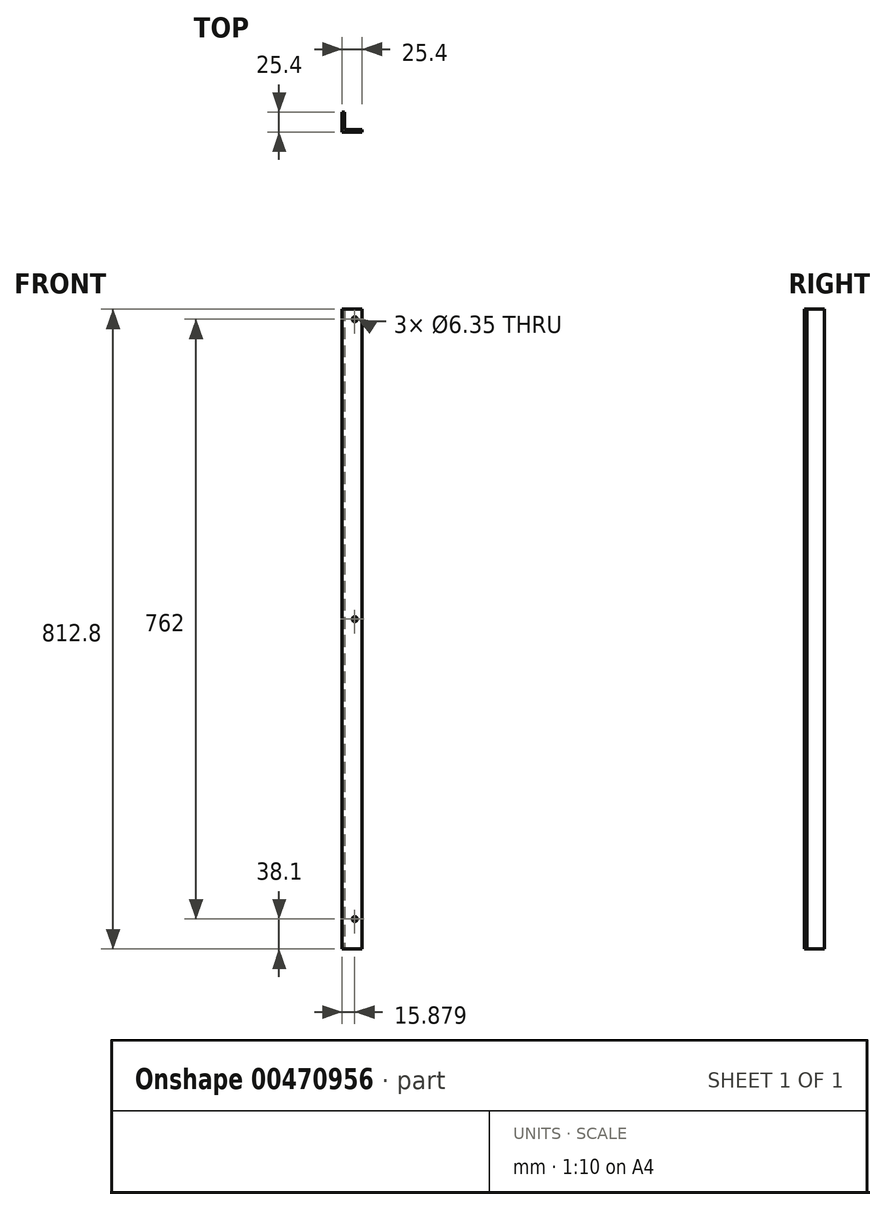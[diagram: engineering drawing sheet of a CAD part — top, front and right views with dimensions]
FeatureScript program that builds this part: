
annotation { "Feature Type Name" : "Feature", "Feature Type Description" : "" }
export const myFeature = defineFeature(function(context is Context, id is Id, definition is map)
    precondition{}
    {
        {
            var Q0;
            Q0=qCreatedBy(makeId("Top.planeOp"),FACE);
            var sketch = newSketch(context, id + "F0", { "sketchPlane" : qUnion([Q0])});
            skLineSegment(sketch, "E0", {"start": v(-9.08, 8.68) * mm, "end": v(-9.08, -16.72) * mm});
            skLineSegment(sketch, "E1", {"start": v(-9.08, -16.72) * mm, "end": v(16.32, -16.72) * mm});
            skLineSegment(sketch, "E2", {"start": v(16.32, -16.72) * mm, "end": v(16.32, -13.54) * mm});
            skLineSegment(sketch, "E3", {"start": v(16.32, -13.54) * mm, "end": v(-5.9, -13.54) * mm});
            skLineSegment(sketch, "E4", {"start": v(-5.9, -13.54) * mm, "end": v(-5.9, 8.68) * mm});
            skLineSegment(sketch, "E5", {"start": v(-5.9, 8.68) * mm, "end": v(-9.08, 8.68) * mm});
            skSolve(sketch);
        }
        {
            var Q0;
            Q0=makeQuery(id+"F0.imprint","IMPRINT",FACE,{"disambiguationData":[TD([[makeQuery(id+"F0.imprint","IMPRINT",EDGE,{"derivedFrom":sQuery(id+"F0.wireOp",EDGE,"E0")}),1.0]])]});
            extrude(context, id + "F1", {"entities" : qUnion([Q0]), "depth" : 812.8 * mm});
        }
        {
            var Q0;
            Q0=makeQuery(id+"F1.opExtrude","SWEPT_FACE",FACE,{"disambiguationData":[OSD([sQuery(id+"F0.wireOp",EDGE,"E1")])]});
            var sketch = newSketch(context, id + "F2", { "sketchPlane" : qUnion([Q0])});
            skPoint(sketch, "E6", {"position": v(6.8, 800.1) * mm});
            skPoint(sketch, "E7", {"position": v(6.8, 419.1) * mm});
            skPoint(sketch, "E8", {"position": v(6.8, 38.1) * mm});
            skSolve(sketch);
        }
        {
            var Q0;
            Q0=sQuery(id+"F2.wireOp",VERTEX,"E6");
            var Q1;
            Q1=sQuery(id+"F2.wireOp",VERTEX,"E7");
            var Q2;
            Q2=sQuery(id+"F2.wireOp",VERTEX,"E8");
            var Q3;
            Q3=makeQuery(id+"F1.opExtrude","SWEPT_BODY",BODY,{"disambiguationData":[OSD([sQuery(id+"F0.wireOp",EDGE,"E0"),sQuery(id+"F0.wireOp",EDGE,"E1"),sQuery(id+"F0.wireOp",EDGE,"E2"),sQuery(id+"F0.wireOp",EDGE,"E3"),sQuery(id+"F0.wireOp",EDGE,"E4"),sQuery(id+"F0.wireOp",EDGE,"E5")])]});
            hole(context, id + "F3", {"style" : HoleStyle.SIMPLE, "endStyle" : HoleEndStyle.BLIND, "holeDiameter" : 6.35 * mm, "holeDepth" : 12.7 * mm, "tappedDepth" : 12.7 * mm, "tapClearance" : 3, "locations" : qUnion([Q0, Q1, Q2]), "scope" : qUnion([Q3])});
        }
    });
